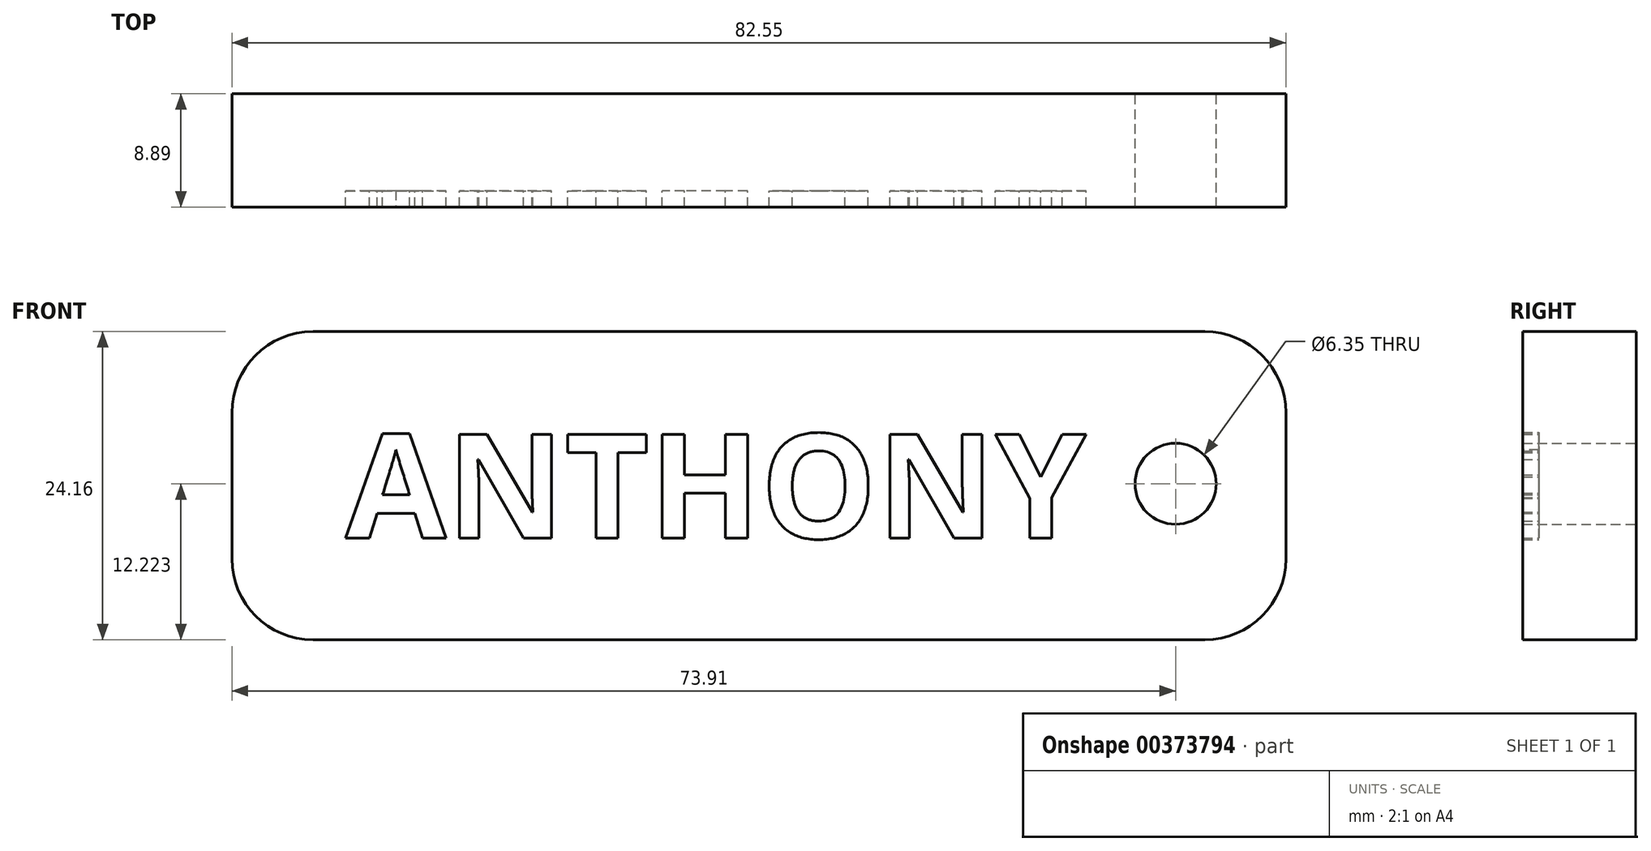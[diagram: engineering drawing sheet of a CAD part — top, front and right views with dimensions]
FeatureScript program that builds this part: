
annotation { "Feature Type Name" : "Feature", "Feature Type Description" : "" }
export const myFeature = defineFeature(function(context is Context, id is Id, definition is map)
    precondition{}
    {
        {
            var Q0;
            Q0=qCreatedBy(makeId("Front.planeOp"),FACE);
            var sketch = newSketch(context, id + "F0", { "sketchPlane" : qUnion([Q0])});
            skLineSegment(sketch, "E0.bottom", {"start": v(-27.88, 7.25) * mm, "end": v(41.97, 7.25) * mm});
            skLineSegment(sketch, "E0.top", {"start": v(-27.88, -16.91) * mm, "end": v(41.97, -16.91) * mm});
            skLineSegment(sketch, "E0.left", {"start": v(-34.23, 0.9) * mm, "end": v(-34.23, -10.56) * mm});
            skLineSegment(sketch, "E0.right", {"start": v(48.32, 0.9) * mm, "end": v(48.32, -10.56) * mm});
            skPoint(sketch, "E1.visualSharp", {"position": v(-34.23, 7.25) * mm});
            skArc(sketch, "E1.filletArc", {"start": v(-27.88, 7.25) * mm, "mid": v(-32.37, 5.39) * mm, "end": v(-34.23, 0.9) * mm});
            skPoint(sketch, "E2.visualSharp", {"position": v(-34.23, -16.91) * mm});
            skArc(sketch, "E2.filletArc", {"start": v(-34.23, -10.56) * mm, "mid": v(-32.37, -15.05) * mm, "end": v(-27.88, -16.91) * mm});
            skPoint(sketch, "E3.visualSharp", {"position": v(48.32, -16.91) * mm});
            skArc(sketch, "E3.filletArc", {"start": v(41.97, -16.91) * mm, "mid": v(46.46, -15.05) * mm, "end": v(48.32, -10.56) * mm});
            skPoint(sketch, "E4.visualSharp", {"position": v(48.32, 7.25) * mm});
            skArc(sketch, "E4.filletArc", {"start": v(48.32, 0.9) * mm, "mid": v(46.46, 5.39) * mm, "end": v(41.97, 7.25) * mm});
            skCircle(sketch, "E5", {"center": v(39.68, -4.69) * mm, "radius": 3.18 * mm});
            skText(sketch, "E6", { "text": "ANTHONY", "fontName": "OpenSans-Bold.ttf"});
            const initialGuessF0  = {"E6": [-0.02532, -0.00895, 1, 0, 0.00822]};
            skSetInitialGuess(sketch, initialGuessF0);
            skSolve(sketch);
        }
        {
            var Q0;
            Q0 = qSketchRegion(id + "F0", true);
            extrude(context, id + "F1", {"entities" : qUnion([Q0]), "depth" : 8.9 * mm});
        }
        {
            var Q0;
            Q0=makeQuery(id+"F0.imprint","IMPRINT",FACE,{"disambiguationData":[TD([[makeQuery(id+"F0.imprint","IMPRINT",EDGE,{"derivedFrom":sQuery(id+"F0.wireOp",EDGE,"E6.sketch_text.stroke-0")}),-1.0]])]});
            var Q1;
            Q1=makeQuery(id+"F0.imprint","IMPRINT",FACE,{"disambiguationData":[TD([[makeQuery(id+"F0.imprint","IMPRINT",EDGE,{"derivedFrom":sQuery(id+"F0.wireOp",EDGE,"E6.sketch_text.stroke-12")}),-1.0]])]});
            var Q2;
            Q2=makeQuery(id+"F0.imprint","IMPRINT",FACE,{"disambiguationData":[TD([[makeQuery(id+"F0.imprint","IMPRINT",EDGE,{"derivedFrom":sQuery(id+"F0.wireOp",EDGE,"E6.sketch_text.stroke-26")}),-1.0]])]});
            var Q3;
            Q3=makeQuery(id+"F0.imprint","IMPRINT",FACE,{"disambiguationData":[TD([[makeQuery(id+"F0.imprint","IMPRINT",EDGE,{"derivedFrom":sQuery(id+"F0.wireOp",EDGE,"E6.sketch_text.stroke-34")}),-1.0]])]});
            var Q4;
            Q4=makeQuery(id+"F0.imprint","IMPRINT",FACE,{"disambiguationData":[TD([[makeQuery(id+"F0.imprint","IMPRINT",EDGE,{"derivedFrom":sQuery(id+"F0.wireOp",EDGE,"E6.sketch_text.stroke-46")}),-1.0]])]});
            var Q5;
            Q5=makeQuery(id+"F0.imprint","IMPRINT",FACE,{"disambiguationData":[TD([[makeQuery(id+"F0.imprint","IMPRINT",EDGE,{"derivedFrom":sQuery(id+"F0.wireOp",EDGE,"E6.sketch_text.stroke-60")}),-1.0]])]});
            var Q6;
            Q6=makeQuery(id+"F0.imprint","IMPRINT",FACE,{"disambiguationData":[TD([[makeQuery(id+"F0.imprint","IMPRINT",EDGE,{"derivedFrom":sQuery(id+"F0.wireOp",EDGE,"E6.sketch_text.stroke-74")}),-1.0]])]});
            extrude(context, id + "F2", {"entities" : qUnion([Q0, Q1, Q2, Q3, Q4, Q5, Q6]), "operationType" : NewBodyOperationType.ADD, "depth" : 7.62 * mm});
        }
        {
            var Q0;
            Q0=makeQuery(id+"F0.imprint","IMPRINT",FACE,{"disambiguationData":[TD([[makeQuery(id+"F0.imprint","IMPRINT",EDGE,{"derivedFrom":sQuery(id+"F0.wireOp",EDGE,"E6.sketch_text.stroke-8")}),1.0]])]});
            var Q1;
            Q1=makeQuery(id+"F0.imprint","IMPRINT",FACE,{"disambiguationData":[TD([[makeQuery(id+"F0.imprint","IMPRINT",EDGE,{"derivedFrom":sQuery(id+"F0.wireOp",EDGE,"E6.sketch_text.stroke-54")}),1.0]])]});
            extrude(context, id + "F3", {"entities" : qUnion([Q0, Q1]), "operationType" : NewBodyOperationType.ADD, "depth" : 8.9 * mm});
        }
    });
